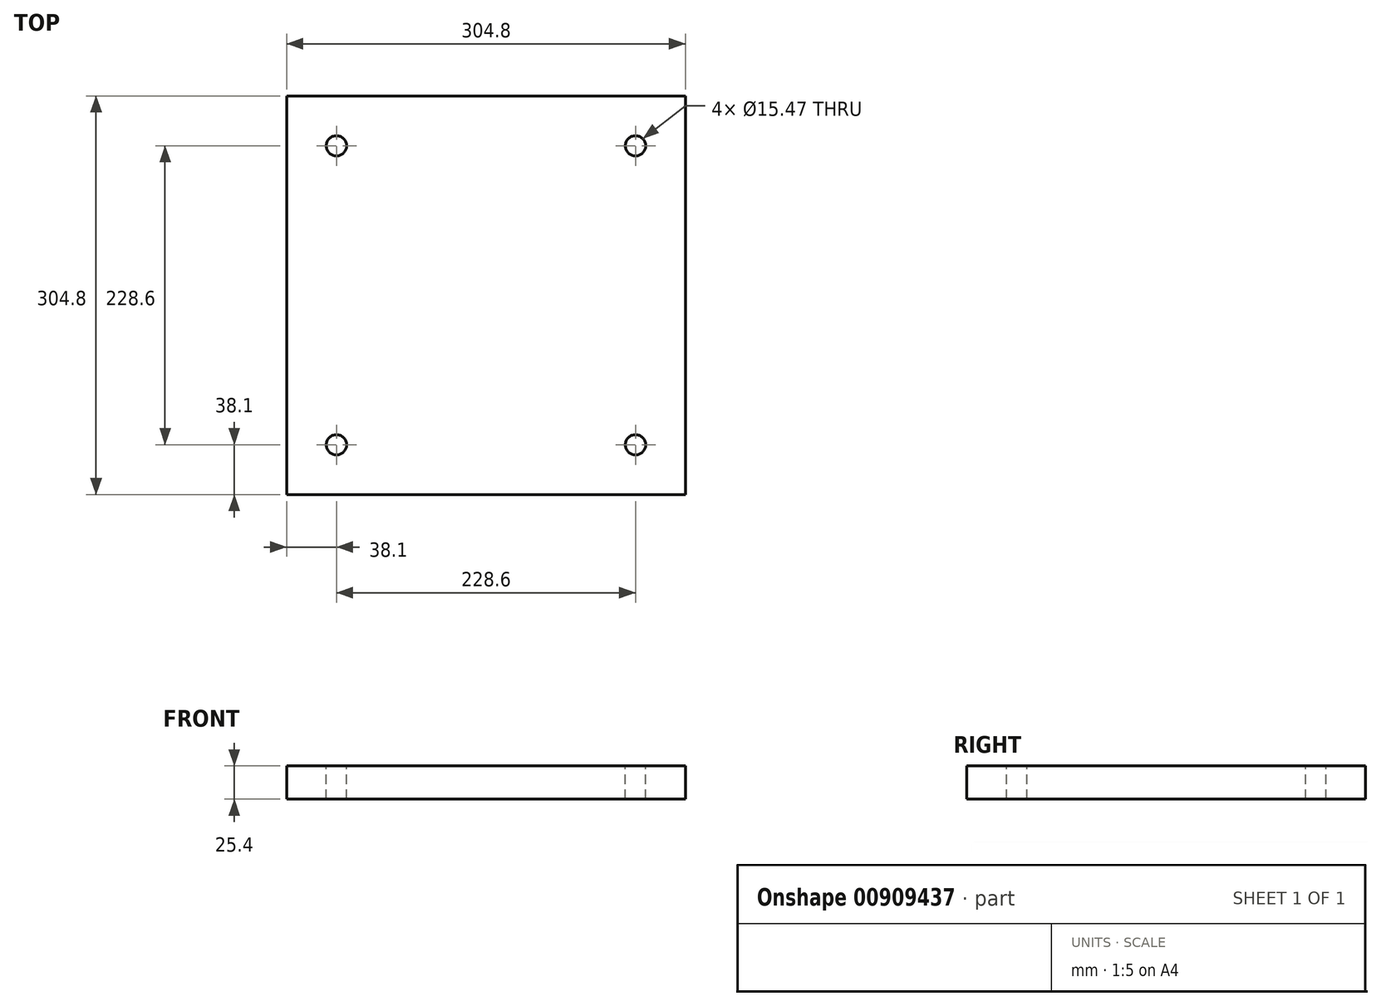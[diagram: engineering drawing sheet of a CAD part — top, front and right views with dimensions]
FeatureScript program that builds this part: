
annotation { "Feature Type Name" : "Feature", "Feature Type Description" : "" }
export const myFeature = defineFeature(function(context is Context, id is Id, definition is map)
    precondition{}
    {
        {
            var Q0;
            Q0=qCreatedBy(makeId("Top.planeOp"),FACE);
            var sketch = newSketch(context, id + "F0", { "sketchPlane" : qUnion([Q0])});
            skLineSegment(sketch, "E0.bottom", {"start": v(-152.4, 152.4) * mm, "end": v(152.4, 152.4) * mm});
            skLineSegment(sketch, "E0.top", {"start": v(-152.4, -152.4) * mm, "end": v(152.4, -152.4) * mm});
            skLineSegment(sketch, "E0.left", {"start": v(-152.4, 152.4) * mm, "end": v(-152.4, -152.4) * mm});
            skLineSegment(sketch, "E0.right", {"start": v(152.4, 152.4) * mm, "end": v(152.4, -152.4) * mm});
            skLineSegment(sketch, "E1", {"start": v(-152.4, 0) * mm, "end": v(0, 0) * mm, "construction": true});
            skLineSegment(sketch, "E2", {"start": v(0, 0) * mm, "end": v(0, 152.4) * mm, "construction": true});
            skSolve(sketch);
        }
        {
            var Q0;
            Q0=qSketchRegion(id+"F0",true);
            extrude(context, id + "F1", {"entities" : qUnion([Q0]), "depth" : 25.4 * mm, "offsetDistance" : 25.4 * mm});
        }
        {
            var Q0;
            Q0=makeQuery(id+"F1.opExtrude","CAP_FACE",FACE,{"disambiguationData":[OSD([sQuery(id+"F0.wireOp",EDGE,"E0.bottom"),sQuery(id+"F0.wireOp",EDGE,"E0.top"),sQuery(id+"F0.wireOp",EDGE,"E0.left"),sQuery(id+"F0.wireOp",EDGE,"E0.right")])],"isStart":false});
            var sketch = newSketch(context, id + "F2", { "sketchPlane" : qUnion([Q0])});
            skLineSegment(sketch, "E3.bottom", {"start": v(-114.3, 114.3) * mm, "end": v(114.3, 114.3) * mm, "construction": true});
            skLineSegment(sketch, "E3.top", {"start": v(-114.3, -114.3) * mm, "end": v(114.3, -114.3) * mm, "construction": true});
            skLineSegment(sketch, "E3.left", {"start": v(-114.3, 114.3) * mm, "end": v(-114.3, -114.3) * mm, "construction": true});
            skLineSegment(sketch, "E3.right", {"start": v(114.3, 114.3) * mm, "end": v(114.3, -114.3) * mm, "construction": true});
            skLineSegment(sketch, "E4", {"start": v(114.3, 0) * mm, "end": v(0, 0) * mm, "construction": true});
            skLineSegment(sketch, "E5", {"start": v(0, 0) * mm, "end": v(0, 114.3) * mm, "construction": true});
            skSolve(sketch);
        }
        {
            var Q0;
            Q0=sQuery(id+"F2.wireOp",VERTEX,"E3.bottom.start");
            var Q1;
            Q1=sQuery(id+"F2.wireOp",VERTEX,"E3.bottom.end");
            var Q2;
            Q2=sQuery(id+"F2.wireOp",VERTEX,"E3.top.end");
            var Q3;
            Q3=sQuery(id+"F2.wireOp",VERTEX,"E3.top.start");
            var Q4;
            Q4=makeQuery(id+"F1.opExtrude","SWEPT_BODY",BODY,{"disambiguationData":[OSD([sQuery(id+"F0.wireOp",EDGE,"E0.bottom"),sQuery(id+"F0.wireOp",EDGE,"E0.top"),sQuery(id+"F0.wireOp",EDGE,"E0.left"),sQuery(id+"F0.wireOp",EDGE,"E0.right")])]});
            hole(context, id + "F3", {"style" : HoleStyle.SIMPLE, "endStyle" : HoleEndStyle.THROUGH, "standardTappedOrClearance" : lookupTablePath({ "fit" : "Loose (ASME)", "standard" : "ANSI", "size" : "1/2", "type" : "Clearance" }), "standardBlindInLast" : lookupTablePath({ "fit" : "Loose", "standard" : "ANSI", "size" : "1/2", "type" : "Clearance" }), "holeDiameter" : 15.47 * mm, "majorDiameter" : 6.35 * mm, "isTappedThrough" : true, "tappedDepth" : 12.7 * mm, "tapClearance" : 3, "locations" : qUnion([Q0, Q1, Q2, Q3]), "scope" : qUnion([Q4])});
        }
    });
